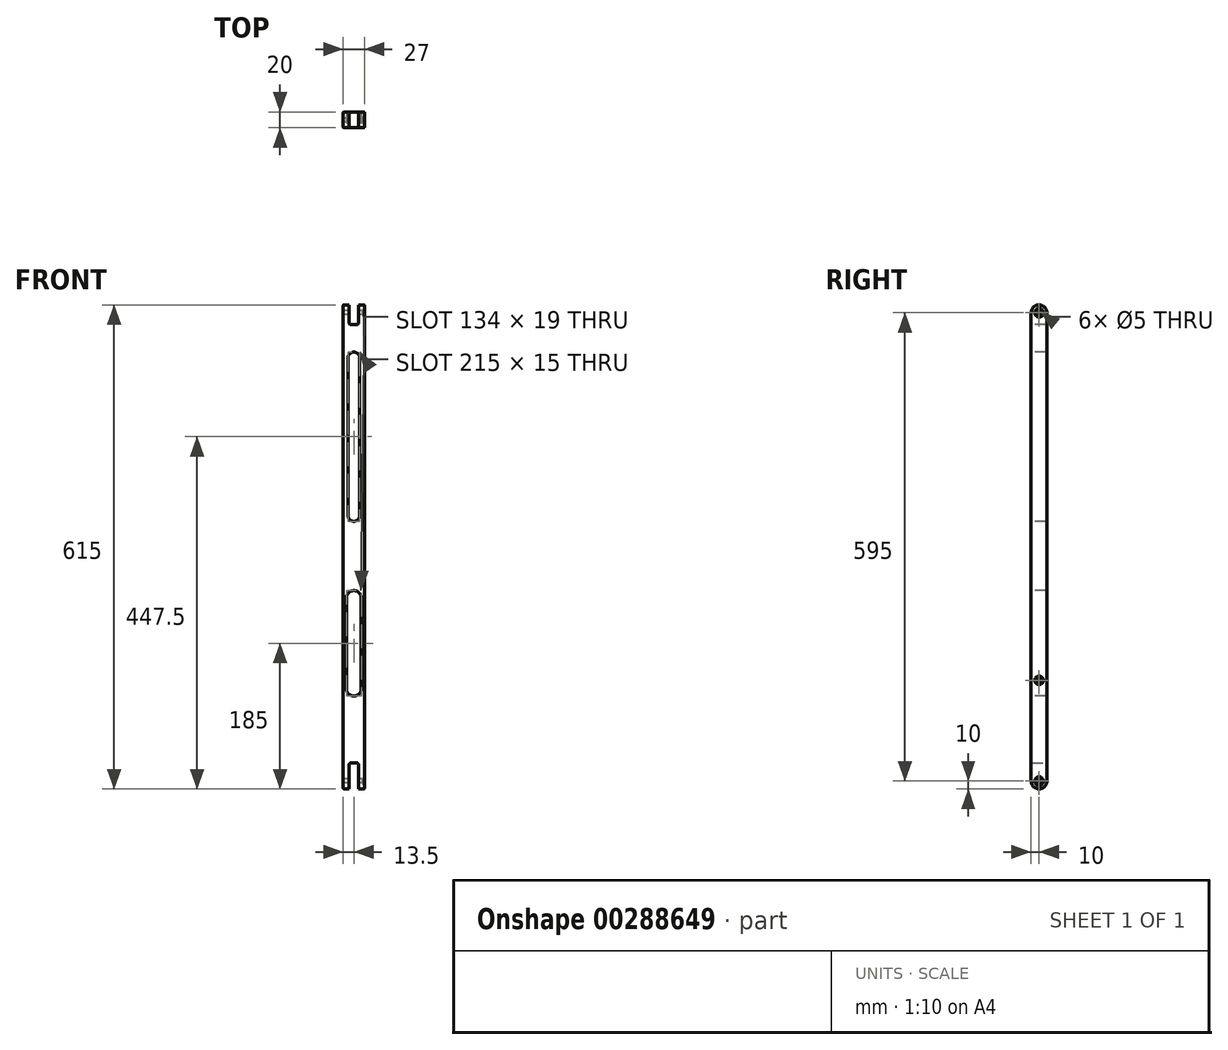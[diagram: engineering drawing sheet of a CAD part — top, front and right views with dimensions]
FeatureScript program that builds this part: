
annotation { "Feature Type Name" : "Feature", "Feature Type Description" : "" }
export const myFeature = defineFeature(function(context is Context, id is Id, definition is map)
    precondition{}
    {
        {
            var Q0;
            Q0=qCreatedBy(makeId("Front.planeOp"),FACE);
            var sketch = newSketch(context, id + "F0", { "sketchPlane" : qUnion([Q0])});
            skLineSegment(sketch, "E0.bottom", {"start": v(13.5, 307.5) * mm, "end": v(-13.5, 307.5) * mm});
            skLineSegment(sketch, "E0.top", {"start": v(13.5, -307.5) * mm, "end": v(-13.5, -307.5) * mm});
            skLineSegment(sketch, "E0.left", {"start": v(13.5, 307.5) * mm, "end": v(13.5, -307.5) * mm});
            skLineSegment(sketch, "E0.right", {"start": v(-13.5, 307.5) * mm, "end": v(-13.5, -307.5) * mm});
            skPoint(sketch, "E0.middle", {"position": v(0, 0) * mm});
            skSolve(sketch);
        }
        {
            var Q0;
            Q0=makeQuery(id+"F0.imprint","IMPRINT",FACE,{"disambiguationData":[TD([[makeQuery(id+"F0.imprint","IMPRINT",EDGE,{"derivedFrom":sQuery(id+"F0.wireOp",EDGE,"E0.bottom")}),1.0]])]});
            extrude(context, id + "F1", {"entities" : qUnion([Q0]), "depth" : 20 * mm});
        }
        {
            var Q0;
            Q0=makeQuery(id+"F1.opExtrude","SWEPT_FACE",FACE,{"disambiguationData":[OSD([sQuery(id+"F0.wireOp",EDGE,"E0.bottom")])]});
            var sketch = newSketch(context, id + "F2", { "sketchPlane" : qUnion([Q0])});
            skLineSegment(sketch, "E1.bottom", {"start": v(-6, 0) * mm, "end": v(6, 0) * mm});
            skLineSegment(sketch, "E1.top", {"start": v(-6, -20) * mm, "end": v(6, -20) * mm});
            skLineSegment(sketch, "E1.left", {"start": v(-6, 0) * mm, "end": v(-6, -20) * mm});
            skLineSegment(sketch, "E1.right", {"start": v(6, 0) * mm, "end": v(6, -20) * mm});
            skSolve(sketch);
        }
        {
            var Q0;
            Q0=makeQuery(id+"F2.imprint","IMPRINT",FACE,{"disambiguationData":[TD([[makeQuery(id+"F2.imprint","IMPRINT",EDGE,{"derivedFrom":sQuery(id+"F2.wireOp",EDGE,"E1.bottom")}),1.0]])]});
            extrude(context, id + "F3", {"entities" : qUnion([Q0]), "operationType" : NewBodyOperationType.REMOVE, "oppositeDirection" : true, "depth" : 25 * mm});
        }
        {
            var Q0;
            Q0=makeQuery(id+"F1.opExtrude","SWEPT_FACE",FACE,{"disambiguationData":[OSD([sQuery(id+"F0.wireOp",EDGE,"E0.top")])]});
            var sketch = newSketch(context, id + "F4", { "sketchPlane" : qUnion([Q0])});
            skLineSegment(sketch, "E2.bottom", {"start": v(-6, 20) * mm, "end": v(6, 20) * mm});
            skLineSegment(sketch, "E2.top", {"start": v(-6, 0) * mm, "end": v(6, 0) * mm});
            skLineSegment(sketch, "E2.left", {"start": v(-6, 20) * mm, "end": v(-6, 0) * mm});
            skLineSegment(sketch, "E2.right", {"start": v(6, 20) * mm, "end": v(6, 0) * mm});
            skSolve(sketch);
        }
        {
            var Q0;
            Q0=makeQuery(id+"F4.imprint","IMPRINT",FACE,{"disambiguationData":[TD([[makeQuery(id+"F4.imprint","IMPRINT",EDGE,{"derivedFrom":sQuery(id+"F4.wireOp",EDGE,"E2.bottom")}),1.0]])]});
            extrude(context, id + "F5", {"entities" : qUnion([Q0]), "operationType" : NewBodyOperationType.REMOVE, "oppositeDirection" : true, "depth" : 33 * mm});
        }
        {
            var Q0;
            {var subQ0=sQuery(id+"F0.wireOp",EDGE,"E0.right");var subQ1=sQuery(id+"F0.wireOp",EDGE,"E0.top");Q0=makeQuery(id+"F5.boolean.opBoolean","SPLIT",EDGE,{"disambiguationData":[TD([makeQuery(id+"F1.opExtrude","SWEPT_FACE",FACE,{"disambiguationData":[OSD([subQ0])]})])],"derivedFrom":makeQuery(id+"F1.opExtrude","CAP_EDGE",EDGE,{"disambiguationData":[OSD([subQ1])],"isStart":true})});}
            var Q1;
            {var subQ0=sQuery(id+"F0.wireOp",EDGE,"E0.left");var subQ1=sQuery(id+"F0.wireOp",EDGE,"E0.top");Q1=makeQuery(id+"F5.boolean.opBoolean","SPLIT",EDGE,{"disambiguationData":[TD([makeQuery(id+"F1.opExtrude","SWEPT_FACE",FACE,{"disambiguationData":[OSD([subQ0])]})])],"derivedFrom":makeQuery(id+"F1.opExtrude","CAP_EDGE",EDGE,{"disambiguationData":[OSD([subQ1])],"isStart":true})});}
            var Q2;
            {var subQ0=sQuery(id+"F0.wireOp",EDGE,"E0.left");var subQ1=sQuery(id+"F0.wireOp",EDGE,"E0.top");Q2=makeQuery(id+"F5.boolean.opBoolean","SPLIT",EDGE,{"disambiguationData":[TD([makeQuery(id+"F1.opExtrude","SWEPT_FACE",FACE,{"disambiguationData":[OSD([subQ0])]})])],"derivedFrom":makeQuery(id+"F1.opExtrude","CAP_EDGE",EDGE,{"disambiguationData":[OSD([subQ1])],"isStart":false})});}
            var Q3;
            {var subQ0=sQuery(id+"F0.wireOp",EDGE,"E0.right");var subQ1=sQuery(id+"F0.wireOp",EDGE,"E0.top");Q3=makeQuery(id+"F5.boolean.opBoolean","SPLIT",EDGE,{"disambiguationData":[TD([makeQuery(id+"F1.opExtrude","SWEPT_FACE",FACE,{"disambiguationData":[OSD([subQ0])]})])],"derivedFrom":makeQuery(id+"F1.opExtrude","CAP_EDGE",EDGE,{"disambiguationData":[OSD([subQ1])],"isStart":false})});}
            var Q4;
            {var subQ0=sQuery(id+"F0.wireOp",EDGE,"E0.bottom");var subQ1=sQuery(id+"F0.wireOp",EDGE,"E0.right");Q4=makeQuery(id+"F3.boolean.opBoolean","SPLIT",EDGE,{"disambiguationData":[TD([makeQuery(id+"F1.opExtrude","SWEPT_FACE",FACE,{"disambiguationData":[OSD([subQ1])]})])],"derivedFrom":makeQuery(id+"F1.opExtrude","CAP_EDGE",EDGE,{"disambiguationData":[OSD([subQ0])],"isStart":false})});}
            var Q5;
            {var subQ0=sQuery(id+"F0.wireOp",EDGE,"E0.bottom");var subQ1=sQuery(id+"F0.wireOp",EDGE,"E0.right");Q5=makeQuery(id+"F3.boolean.opBoolean","SPLIT",EDGE,{"disambiguationData":[TD([makeQuery(id+"F1.opExtrude","SWEPT_FACE",FACE,{"disambiguationData":[OSD([subQ1])]})])],"derivedFrom":makeQuery(id+"F1.opExtrude","CAP_EDGE",EDGE,{"disambiguationData":[OSD([subQ0])],"isStart":true})});}
            var Q6;
            {var subQ0=sQuery(id+"F0.wireOp",EDGE,"E0.bottom");var subQ1=sQuery(id+"F0.wireOp",EDGE,"E0.left");Q6=makeQuery(id+"F3.boolean.opBoolean","SPLIT",EDGE,{"disambiguationData":[TD([makeQuery(id+"F1.opExtrude","SWEPT_FACE",FACE,{"disambiguationData":[OSD([subQ1])]})])],"derivedFrom":makeQuery(id+"F1.opExtrude","CAP_EDGE",EDGE,{"disambiguationData":[OSD([subQ0])],"isStart":true})});}
            var Q7;
            {var subQ0=sQuery(id+"F0.wireOp",EDGE,"E0.bottom");var subQ1=sQuery(id+"F0.wireOp",EDGE,"E0.left");Q7=makeQuery(id+"F3.boolean.opBoolean","SPLIT",EDGE,{"disambiguationData":[TD([makeQuery(id+"F1.opExtrude","SWEPT_FACE",FACE,{"disambiguationData":[OSD([subQ1])]})])],"derivedFrom":makeQuery(id+"F1.opExtrude","CAP_EDGE",EDGE,{"disambiguationData":[OSD([subQ0])],"isStart":false})});}
            fillet(context, id + "F6", {"entities" : qUnion([Q0, Q1, Q2, Q3, Q4, Q5, Q6, Q7]), "radius" : 10 * mm, "tangentPropagation" : true, "allowEdgeOverflow" : false});
        }
        {
            var Q0;
            Q0=makeQuery(id+"F1.opExtrude","SWEPT_FACE",FACE,{"disambiguationData":[OSD([sQuery(id+"F0.wireOp",EDGE,"E0.right")])]});
            var sketch = newSketch(context, id + "F7", { "sketchPlane" : qUnion([Q0])});
            skCircle(sketch, "E3", {"center": v(10, 297.5) * mm, "radius": 2.5 * mm});
            skCircle(sketch, "E4", {"center": v(10, -297.5) * mm, "radius": 2.5 * mm});
            skSolve(sketch);
        }
        {
            var Q0;
            Q0 = qSketchRegion(id + "F7", true);
            extrude(context, id + "F8", {"entities" : qUnion([Q0]), "operationType" : NewBodyOperationType.REMOVE, "oppositeDirection" : true, "depth" : 30 * mm});
        }
        {
            var Q0;
            Q0=makeQuery(id+"F1.opExtrude","CAP_FACE",FACE,{"disambiguationData":[OSD([sQuery(id+"F0.wireOp",EDGE,"E0.bottom"),sQuery(id+"F0.wireOp",EDGE,"E0.top"),sQuery(id+"F0.wireOp",EDGE,"E0.left"),sQuery(id+"F0.wireOp",EDGE,"E0.right")])],"isStart":false});
            var sketch = newSketch(context, id + "F9", { "sketchPlane" : qUnion([Q0])});
            skLineSegment(sketch, "E5.left", {"start": v(-9.5, -65) * mm, "end": v(-9.5, -180) * mm});
            skLineSegment(sketch, "E5.right", {"start": v(9.5, -65) * mm, "end": v(9.5, -180) * mm});
            skArc(sketch, "E6", {"start": v(-9.5, -65) * mm, "mid": v(0, -55.5) * mm, "end": v(9.5, -65) * mm});
            skArc(sketch, "E7", {"start": v(9.5, -180) * mm, "mid": v(0, -189.5) * mm, "end": v(-9.5, -180) * mm});
            skSolve(sketch);
        }
        {
            var Q0;
            Q0=makeQuery(id+"F9.imprint","IMPRINT",FACE,{"disambiguationData":[TD([[makeQuery(id+"F9.imprint","IMPRINT",EDGE,{"derivedFrom":sQuery(id+"F9.wireOp",EDGE,"E5.left")}),1.0]])]});
            extrude(context, id + "F10", {"entities" : qUnion([Q0]), "operationType" : NewBodyOperationType.REMOVE, "oppositeDirection" : true, "depth" : 25 * mm, "offsetDistance" : 25 * mm});
        }
        {
            var Q0;
            Q0=makeQuery(id+"F1.opExtrude","SWEPT_FACE",FACE,{"disambiguationData":[OSD([sQuery(id+"F0.wireOp",EDGE,"E0.right")])]});
            var sketch = newSketch(context, id + "F11", { "sketchPlane" : qUnion([Q0])});
            skCircle(sketch, "E8", {"center": v(10, -169.5) * mm, "radius": 2.5 * mm});
            skSolve(sketch);
        }
        {
            var Q0;
            Q0=makeQuery(id+"F11.imprint","IMPRINT",FACE,{"disambiguationData":[TD([[makeQuery(id+"F11.imprint","IMPRINT",EDGE,{"derivedFrom":sQuery(id+"F11.wireOp",EDGE,"E8")}),1.0]])]});
            var Q1;
            Q1=sQuery(id+"F11.wireOp",EDGE,"E8");
            extrude(context, id + "F12", {"entities" : qUnion([Q0]), "operationType" : NewBodyOperationType.REMOVE, "surfaceEntities" : qUnion([Q1]), "oppositeDirection" : true, "depth" : 30 * mm});
        }
        {
            var Q0;
            Q0=makeQuery(id+"F1.opExtrude","CAP_FACE",FACE,{"disambiguationData":[OSD([sQuery(id+"F0.wireOp",EDGE,"E0.bottom"),sQuery(id+"F0.wireOp",EDGE,"E0.top"),sQuery(id+"F0.wireOp",EDGE,"E0.left"),sQuery(id+"F0.wireOp",EDGE,"E0.right")])],"isStart":false});
            var sketch = newSketch(context, id + "F13", { "sketchPlane" : qUnion([Q0])});
            skLineSegment(sketch, "E9.left", {"start": v(-7.5, 240) * mm, "end": v(-7.5, 40) * mm});
            skLineSegment(sketch, "E9.right", {"start": v(7.5, 240) * mm, "end": v(7.5, 40) * mm});
            skArc(sketch, "E10", {"start": v(-7.5, 240) * mm, "mid": v(0, 247.5) * mm, "end": v(7.5, 240) * mm});
            skArc(sketch, "E11", {"start": v(7.5, 40) * mm, "mid": v(0, 32.5) * mm, "end": v(-7.5, 40) * mm});
            skSolve(sketch);
        }
        {
            var Q0;
            Q0=makeQuery(id+"F13.imprint","IMPRINT",FACE,{"disambiguationData":[TD([[makeQuery(id+"F13.imprint","IMPRINT",EDGE,{"derivedFrom":sQuery(id+"F13.wireOp",EDGE,"E9.left")}),1.0]])]});
            extrude(context, id + "F14", {"entities" : qUnion([Q0]), "operationType" : NewBodyOperationType.REMOVE, "oppositeDirection" : true, "depth" : 25 * mm, "offsetDistance" : 25 * mm});
        }
        {
            var Q0;
            Q0=makeQuery(id+"F1.opExtrude","CAP_EDGE",EDGE,{"disambiguationData":[OSD([sQuery(id+"F0.wireOp",EDGE,"E0.left")])],"isStart":false});
            var Q1;
            Q1=makeQuery(id+"F1.opExtrude","CAP_EDGE",EDGE,{"disambiguationData":[OSD([sQuery(id+"F0.wireOp",EDGE,"E0.right")])],"isStart":false});
            fillet(context, id + "F15", {"entities" : qUnion([Q0, Q1]), "radius" : 1 * mm, "tangentPropagation" : true, "allowEdgeOverflow" : false});
        }
        {
            var Q0;
            Q0=makeQuery(id+"F8.boolean.opBoolean","INTERSECT",EDGE,{"derivedFrom":[makeQuery(id+"F1.opExtrude","SWEPT_FACE",FACE,{"disambiguationData":[OSD([sQuery(id+"F0.wireOp",EDGE,"E0.left")])]}),makeQuery(id+"F8.opExtrude","SWEPT_FACE",FACE,{"disambiguationData":[OSD([sQuery(id+"F7.wireOp",EDGE,"E3")])]})]});
            var Q1;
            Q1=makeQuery(id+"F12.boolean.opBoolean","INTERSECT",EDGE,{"derivedFrom":[makeQuery(id+"F1.opExtrude","SWEPT_FACE",FACE,{"disambiguationData":[OSD([sQuery(id+"F0.wireOp",EDGE,"E0.left")])]}),makeQuery(id+"F12.opExtrude","SWEPT_FACE",FACE,{"disambiguationData":[OSD([sQuery(id+"F11.wireOp",EDGE,"E8")])]})]});
            var Q2;
            Q2=makeQuery(id+"F8.boolean.opBoolean","INTERSECT",EDGE,{"derivedFrom":[makeQuery(id+"F1.opExtrude","SWEPT_FACE",FACE,{"disambiguationData":[OSD([sQuery(id+"F0.wireOp",EDGE,"E0.left")])]}),makeQuery(id+"F8.opExtrude","SWEPT_FACE",FACE,{"disambiguationData":[OSD([sQuery(id+"F7.wireOp",EDGE,"E4")])]})]});
            chamfer(context, id + "F16", {"entities" : qUnion([Q0, Q1, Q2]), "width" : 3 * mm, "tangentPropagation" : true});
        }
        {
            var Q0;
            Q0=makeQuery(id+"F3.boolean.opBoolean","COPY",EDGE,{"derivedFrom":makeQuery(id+"F3.opExtrude","CAP_EDGE",EDGE,{"disambiguationData":[OSD([sQuery(id+"F2.wireOp",EDGE,"E1.left")])],"isStart":false})});
            var Q1;
            Q1=makeQuery(id+"F3.boolean.opBoolean","COPY",EDGE,{"derivedFrom":makeQuery(id+"F3.opExtrude","CAP_EDGE",EDGE,{"disambiguationData":[OSD([sQuery(id+"F2.wireOp",EDGE,"E1.right")])],"isStart":false})});
            var Q2;
            Q2=makeQuery(id+"F5.boolean.opBoolean","COPY",EDGE,{"derivedFrom":makeQuery(id+"F5.opExtrude","CAP_EDGE",EDGE,{"disambiguationData":[OSD([sQuery(id+"F4.wireOp",EDGE,"E2.right")])],"isStart":false})});
            var Q3;
            Q3=makeQuery(id+"F5.boolean.opBoolean","COPY",EDGE,{"derivedFrom":makeQuery(id+"F5.opExtrude","CAP_EDGE",EDGE,{"disambiguationData":[OSD([sQuery(id+"F4.wireOp",EDGE,"E2.left")])],"isStart":false})});
            fillet(context, id + "F17", {"entities" : qUnion([Q0, Q1, Q2, Q3]), "radius" : 2 * mm, "tangentPropagation" : true, "allowEdgeOverflow" : false});
        }
    });
